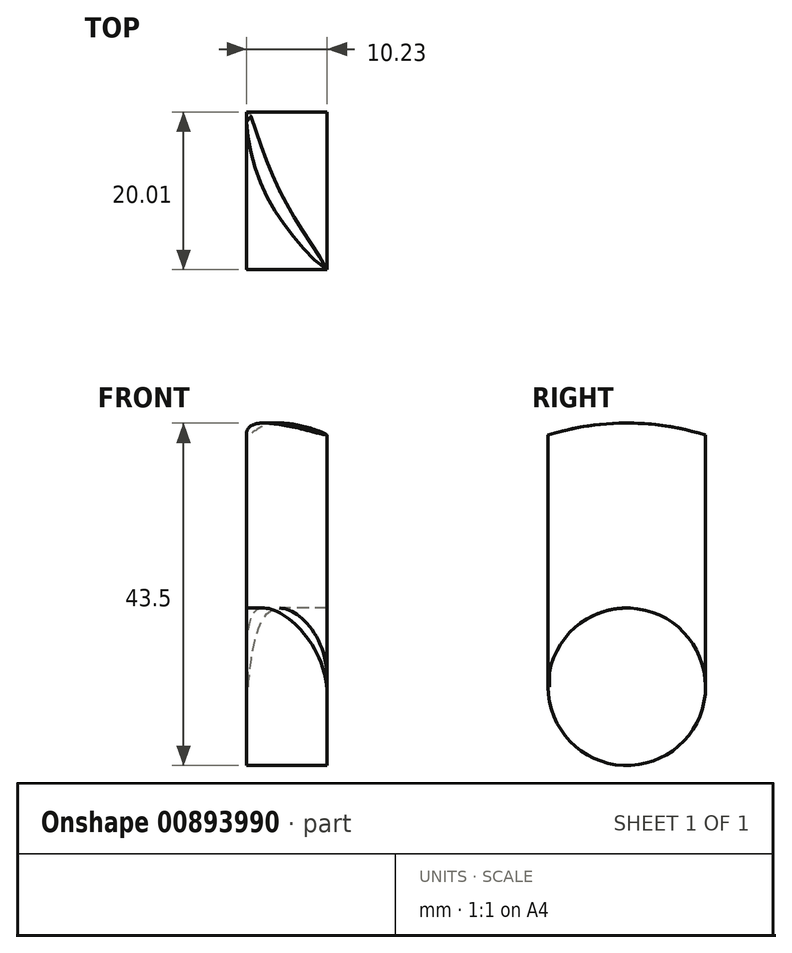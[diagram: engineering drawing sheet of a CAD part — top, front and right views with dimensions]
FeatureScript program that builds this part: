
annotation { "Feature Type Name" : "Feature", "Feature Type Description" : "" }
export const myFeature = defineFeature(function(context is Context, id is Id, definition is map)
    precondition{}
    {
        {
            var Q0;
            Q0=qCreatedBy(makeId("Top.planeOp"),FACE);
            var sketch = newSketch(context, id + "F0", { "sketchPlane" : qUnion([Q0])});
            skFitSpline(sketch, "E0", {"points": [v(7, -10) * mm, v(1, 0) * mm, v(-3, 10) * mm, v(-1, 0) * mm, v(7, -10) * mm]});
            skSolve(sketch);
        }
        {
            var Q0;
            Q0=makeQuery(id+"F0.imprint","IMPRINT",FACE,{"disambiguationData":[TD([[makeQuery(id+"F0.imprint","IMPRINT",EDGE,{"derivedFrom":sQuery(id+"F0.wireOp",EDGE,"E0")}),1.0]])]});
            var Q1;
            Q1=makeQuery(id+"F0.imprint","IMPRINT",FACE,{"disambiguationData":[TD([[makeQuery(id+"F0.imprint","IMPRINT",EDGE,{"derivedFrom":sQuery(id+"F0.wireOp",EDGE,"VSYTqqWi-rlza-7QPz-apfo-Vg90DQTrZlbX.bottom")}),-1.0]])]});
            extrude(context, id + "F1", {"entities" : qUnion([Q0, Q1]), "depth" : 36 * mm, "offsetDistance" : 25 * mm});
        }
        {
            var Q0;
            Q0=qCreatedBy(makeId("Right.planeOp"),FACE);
            var sketch = newSketch(context, id + "F2", { "sketchPlane" : qUnion([Q0])});
            skCircle(sketch, "E1", {"center": v(0, 0) * mm, "radius": 10 * mm});
            skSolve(sketch);
        }
        {
            var Q0;
            Q0=qSketchRegion(id+"F2",true);
            extrude(context, id + "F3", {"entities" : qUnion([Q0]), "operationType" : NewBodyOperationType.ADD, "depth" : 7 * mm, "offsetDistance" : 25 * mm});
        }
        {
            var Q0;
            Q0=qSketchRegion(id+"F2",true);
            extrude(context, id + "F4", {"entities" : qUnion([Q0]), "operationType" : NewBodyOperationType.ADD, "oppositeDirection" : true, "depth" : 3.2 * mm, "offsetDistance" : 25 * mm});
        }
        {
            var Q0;
            Q0=qCreatedBy(makeId("Front.planeOp"),FACE);
            var sketch = newSketch(context, id + "F5", { "sketchPlane" : qUnion([Q0])});
            skLineSegment(sketch, "E2", {"start": v(0, 0) * mm, "end": v(-12.76, 0) * mm, "construction": true});
            skSolve(sketch);
        }
        {
            var Q0;
            Q0=makeQuery(id+"F4.opExtrude","CAP_FACE",FACE,{"disambiguationData":[OSD([sQuery(id+"F2.wireOp",EDGE,"E1")])],"isStart":false});
            var sketch = newSketch(context, id + "F6", { "sketchPlane" : qUnion([Q0])});
            skCircle(sketch, "E3", {"center": v(0, 0) * mm, "radius": 33.5 * mm});
            skCircle(sketch, "E4", {"center": v(0, 0) * mm, "radius": 40 * mm});
            skSolve(sketch);
        }
        {
            var Q0;
            Q0=makeQuery(id+"F6.imprint","IMPRINT",FACE,{"disambiguationData":[TD([[makeQuery(id+"F6.imprint","IMPRINT",EDGE,{"derivedFrom":sQuery(id+"F6.wireOp",EDGE,"E3")}),-1.0]])]});
            extrude(context, id + "F7", {"entities" : qUnion([Q0]), "operationType" : NewBodyOperationType.REMOVE, "oppositeDirection" : true, "depth" : 25 * mm, "offsetDistance" : 25 * mm});
        }
    });
